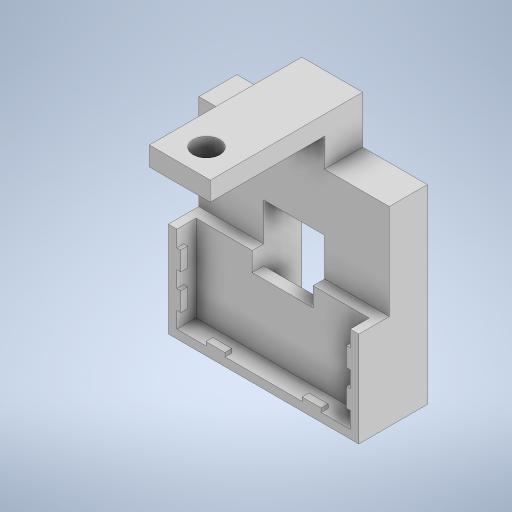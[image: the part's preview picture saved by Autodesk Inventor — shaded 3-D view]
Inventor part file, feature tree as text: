
AUTODESK INVENTOR PART (.ipt)
format: ipt  version: 2023 (Build 270158000, 158)  size: 360,448 bytes
history: native  units: in
note: dims shown in document units (in); Inventor stores cm internally (conversion verified against a paired STEP export)
features: extrude x8, sketch x8
ambient origin geometry x8: Origin, YZ Plane, XZ Plane, XY Plane, X Axis, Y Axis, Z Axis, Center Point
bodies: Solid1 (feature_tree)
feature tree (16):
  extrude  "Extrusion1"  TaperAngle=0.0deg  [1 undecoded]
  extrude  "Extrusion2"  Depth=0.1181in TaperAngle=0.0deg
  extrude  "Extrusion3"  TaperAngle=0.0deg  [1 undecoded]
  extrude  "Extrusion4"  Depth=0.1969in TaperAngle=0.0deg
  extrude  "Extrusion5"  Depth=0.1969in
  extrude  "Extrusion6"  Depth=0.0394in TaperAngle=0.0deg
  extrude  "Extrusion7"  Depth=0.3937in TaperAngle=0.0deg
  extrude  "Extrusion15"  Depth=0.1969in
  sketch  "Sketch1"  dims[d0=1.9685in d1=0.0in]
  sketch  "Sketch2"  dims[d2=0.9843in d3=0.1181in d4=0.0in]
  sketch  "Sketch3"  dims[d5=1.7913in d6=0.0in]
  sketch  "Sketch4"  dims[d7=0.8071in d8=0.1969in d9=0.0in]
  sketch  "Sketch5"  dims[d10=0.1969in d11=0.1969in]
  sketch  "Sketch6"  dims[d12=0.0394in d13=0.0in d14=0.0394in d15=0.0in]
  sketch  "Sketch7"  dims[d22=0.0394in d23=0.0in d26=0.3937in d27=0.0in]
  sketch  "Sketch18"  dims[d28=0.0709in d31=0.1969in d32=0.0709in d33=0.1969in d34=0.0709in d35=0.6299in d36=0.1969in d37=0.0in d38=0.0in d41=0.6693in d42=1.9685in d43=0.6693in d44=1.9685in d47=0.6299in d49=0.0in d86=1.1811in d87=0.2756in d88=0.2756in d89=0.1969in d90=0.0in d39=0.0197in d40=0.0344in]
note: 2 required parameter values undecoded (feature->parameter linkage not recoverable at this tier; creation-order binding heuristic only, values carry confidence <= 0.55)
